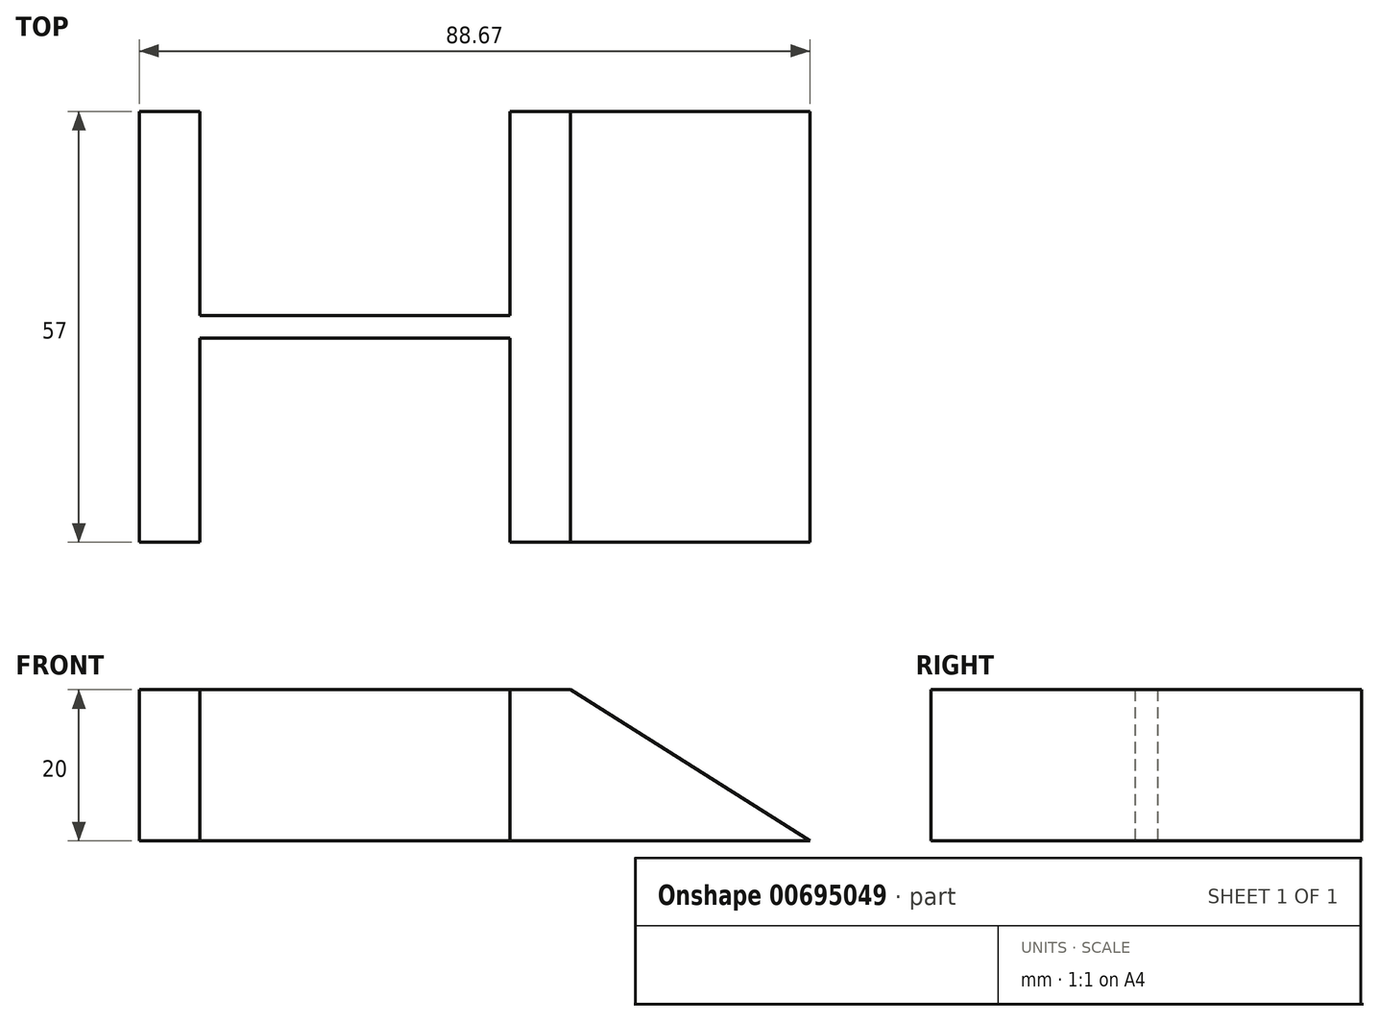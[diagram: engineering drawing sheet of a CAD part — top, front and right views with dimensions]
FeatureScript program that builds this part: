
annotation { "Feature Type Name" : "Feature", "Feature Type Description" : "" }
export const myFeature = defineFeature(function(context is Context, id is Id, definition is map)
    precondition{}
    {
        {
            var Q0;
            Q0=qCreatedBy(makeId("Top.planeOp"),FACE);
            var sketch = newSketch(context, id + "F0", { "sketchPlane" : qUnion([Q0])});
            skLineSegment(sketch, "E0", {"start": v(-37.17, 30) * mm, "end": v(-37.17, -27) * mm});
            skLineSegment(sketch, "E1", {"start": v(-37.17, 30) * mm, "end": v(-29.17, 30) * mm});
            skLineSegment(sketch, "E2", {"start": v(-29.17, 30) * mm, "end": v(-29.17, 3) * mm});
            skLineSegment(sketch, "E3", {"start": v(-29.17, 3) * mm, "end": v(11.83, 3) * mm});
            skLineSegment(sketch, "E4", {"start": v(11.83, 3) * mm, "end": v(11.83, 30) * mm});
            skLineSegment(sketch, "E5", {"start": v(11.83, 30) * mm, "end": v(19.83, 30) * mm});
            skLineSegment(sketch, "E6", {"start": v(-37.17, -27) * mm, "end": v(-29.17, -27) * mm});
            skLineSegment(sketch, "E7", {"start": v(-29.17, -27) * mm, "end": v(-29.17, 0) * mm});
            skLineSegment(sketch, "E8", {"start": v(19.83, -27) * mm, "end": v(11.83, -27) * mm});
            skLineSegment(sketch, "E9", {"start": v(11.83, -27) * mm, "end": v(11.83, 0) * mm});
            skLineSegment(sketch, "E10", {"start": v(-29.17, 0) * mm, "end": v(11.83, 0) * mm});
            skLineSegment(sketch, "E11", {"start": v(19.83, 30) * mm, "end": v(19.83, -27) * mm});
            skSolve(sketch);
        }
        {
            var Q0;
            Q0 = qSketchRegion(id + "F0", true);
            extrude(context, id + "F1", {"entities" : qUnion([Q0]), "depth" : 20 * mm, "offsetDistance" : 25 * mm});
        }
        {
            var Q0;
            Q0=makeQuery(id+"F1.opExtrude","SWEPT_FACE",FACE,{"disambiguationData":[OSD([sQuery(id+"F0.wireOp",EDGE,"E8")])]});
            var sketch = newSketch(context, id + "F2", { "sketchPlane" : qUnion([Q0])});
            skLineSegment(sketch, "E12", {"start": v(19.83, 0) * mm, "end": v(19.83, 20) * mm});
            skLineSegment(sketch, "E13", {"start": v(19.83, 20) * mm, "end": v(51.5, 0) * mm});
            skLineSegment(sketch, "E14", {"start": v(51.5, 0) * mm, "end": v(19.83, 0) * mm});
            skSolve(sketch);
        }
        {
            var Q0;
            Q0 = qSketchRegion(id + "F2", true);
            extrude(context, id + "F3", {"entities" : qUnion([Q0]), "operationType" : NewBodyOperationType.ADD, "oppositeDirection" : true, "depth" : 57 * mm, "offsetDistance" : 25 * mm});
        }
    });
